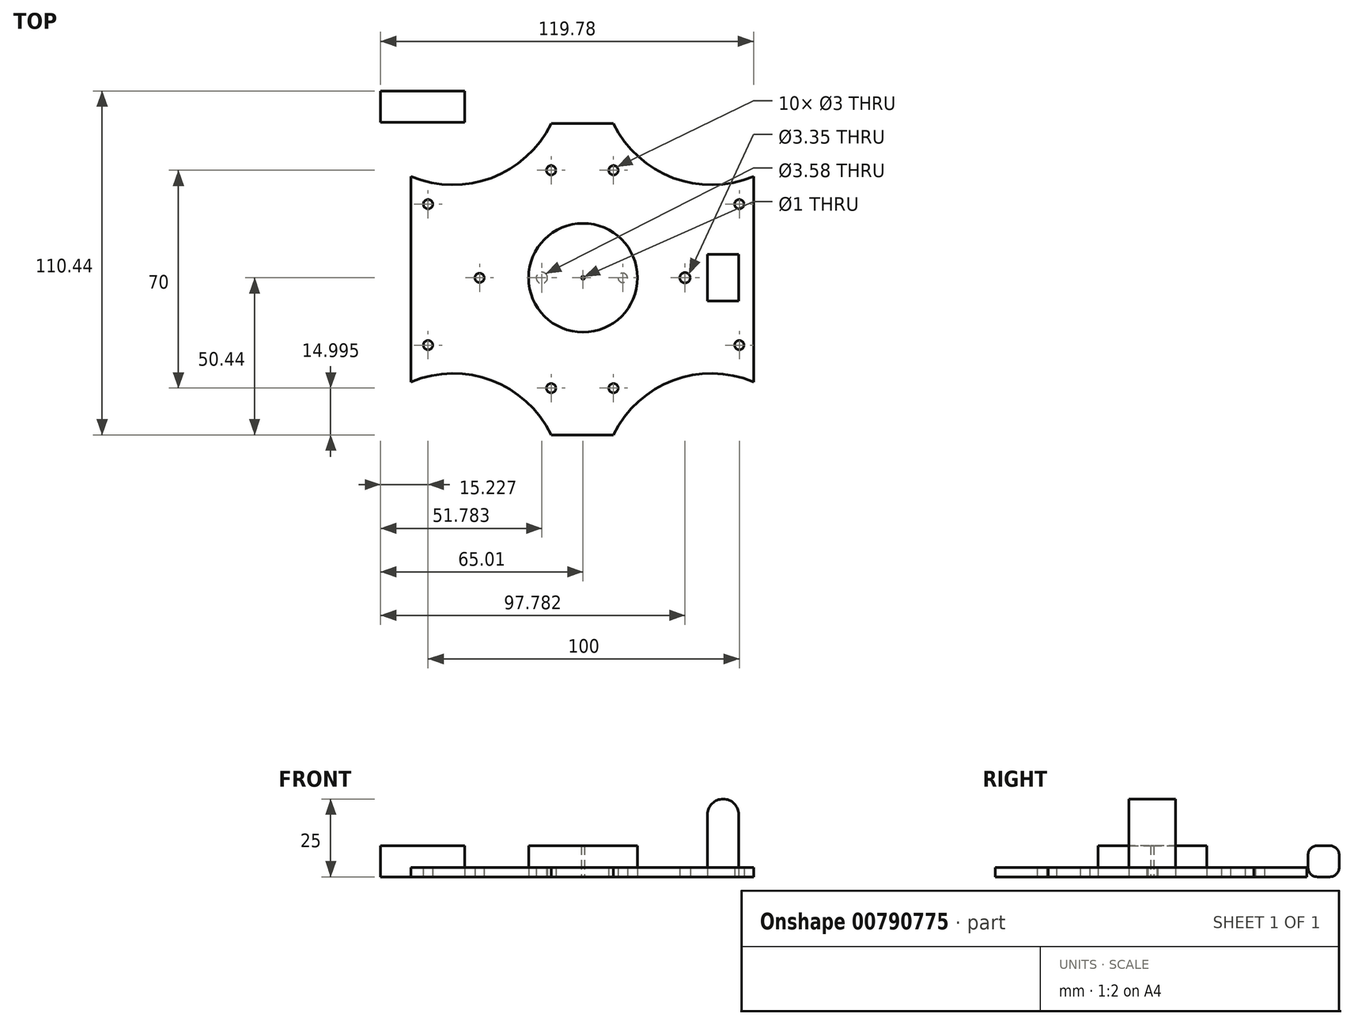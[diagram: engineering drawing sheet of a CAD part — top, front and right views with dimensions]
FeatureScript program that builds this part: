
annotation { "Feature Type Name" : "Feature", "Feature Type Description" : "" }
export const myFeature = defineFeature(function(context is Context, id is Id, definition is map)
    precondition{}
    {
        {
            var Q0;
            Q0=qCreatedBy(makeId("Top.planeOp"),FACE);
            var sketch = newSketch(context, id + "F0", { "sketchPlane" : qUnion([Q0])});
            skCircle(sketch, "E0", {"center": v(0, 0) * mm, "radius": 17.5 * mm});
            skCircle(sketch, "E1", {"center": v(0, 0) * mm, "radius": 0.5 * mm});
            skSolve(sketch);
        }
        {
            var Q0;
            Q0=makeQuery(id+"F0.imprint","IMPRINT",FACE,{"disambiguationData":[TD([[makeQuery(id+"F0.imprint","IMPRINT",EDGE,{"derivedFrom":sQuery(id+"F0.wireOp",EDGE,"E0")}),1.0]])]});
            extrude(context, id + "F1", {"entities" : qUnion([Q0]), "depth" : 10 * mm, "offsetDistance" : 25 * mm});
        }
        {
            var Q0;
            Q0=qCreatedBy(makeId("Top.planeOp"),FACE);
            var sketch = newSketch(context, id + "F2", { "sketchPlane" : qUnion([Q0])});
            skLineSegment(sketch, "E2.bottom", {"start": v(-38.01, 50) * mm, "end": v(-65.01, 50) * mm});
            skLineSegment(sketch, "E2.top", {"start": v(-38.01, 60) * mm, "end": v(-65.01, 60) * mm});
            skLineSegment(sketch, "E2.left", {"start": v(-38.01, 50) * mm, "end": v(-38.01, 60) * mm});
            skLineSegment(sketch, "E2.right", {"start": v(-65.01, 50) * mm, "end": v(-65.01, 60) * mm});
            skPoint(sketch, "E2.middle", {"position": v(-51.51, 55) * mm});
            skSolve(sketch);
        }
        {
            var Q0;
            Q0=makeQuery(id+"F2.imprint","IMPRINT",FACE,{"disambiguationData":[TD([[makeQuery(id+"F2.imprint","IMPRINT",EDGE,{"derivedFrom":sQuery(id+"F2.wireOp",EDGE,"E2.bottom")}),-1.0]])]});
            extrude(context, id + "F3", {"entities" : qUnion([Q0]), "depth" : 10 * mm, "offsetDistance" : 25 * mm});
        }
        {
            var Q0;
            Q0=makeQuery(id+"F3.opExtrude","CAP_EDGE",EDGE,{"disambiguationData":[OSD([sQuery(id+"F2.wireOp",EDGE,"E2.top")])],"isStart":false});
            var Q1;
            Q1=makeQuery(id+"F3.opExtrude","CAP_EDGE",EDGE,{"disambiguationData":[OSD([sQuery(id+"F2.wireOp",EDGE,"E2.bottom")])],"isStart":false});
            var Q2;
            Q2=makeQuery(id+"F3.opExtrude","CAP_EDGE",EDGE,{"disambiguationData":[OSD([sQuery(id+"F2.wireOp",EDGE,"E2.bottom")])],"isStart":true});
            var Q3;
            Q3=makeQuery(id+"F3.opExtrude","CAP_EDGE",EDGE,{"disambiguationData":[OSD([sQuery(id+"F2.wireOp",EDGE,"E2.top")])],"isStart":true});
            fillet(context, id + "F4", {"entities" : qUnion([Q0, Q1, Q2, Q3]), "radius" : 3 * mm, "tangentPropagation" : true, "allowEdgeOverflow" : false});
        }
        {
            var Q0;
            Q0=qCreatedBy(makeId("Top.planeOp"),FACE);
            var sketch = newSketch(context, id + "F5", { "sketchPlane" : qUnion([Q0])});
            skLineSegment(sketch, "E3.bottom", {"start": v(9.77, 49.56) * mm, "end": v(-10.23, 49.56) * mm});
            skLineSegment(sketch, "E3.top", {"start": v(9.77, -50.44) * mm, "end": v(-10.23, -50.44) * mm});
            skLineSegment(sketch, "E3.left", {"start": v(54.77, 32.56) * mm, "end": v(54.77, -33.44) * mm});
            skLineSegment(sketch, "E3.right", {"start": v(-55.23, 32.56) * mm, "end": v(-55.23, -33.44) * mm});
            skPoint(sketch, "E3.middle", {"position": v(0, 0) * mm});
            skPoint(sketch, "E4", {"position": v(-10.23, 49.56) * mm});
            skPoint(sketch, "E5", {"position": v(9.77, 49.56) * mm});
            skPoint(sketch, "E6", {"position": v(-10.23, -50.44) * mm});
            skPoint(sketch, "E7", {"position": v(9.77, -50.44) * mm});
            skPoint(sketch, "E8", {"position": v(54.77, 32.56) * mm});
            skPoint(sketch, "E9", {"position": v(54.77, -33.44) * mm});
            skPoint(sketch, "E10", {"position": v(-55.23, -33.44) * mm});
            skArc(sketch, "E11", {"start": v(-55.23, 32.56) * mm, "mid": v(-29.34, 32.1) * mm, "end": v(-10.23, 49.56) * mm});
            skArc(sketch, "E12", {"start": v(9.77, 49.56) * mm, "mid": v(28.89, 32.1) * mm, "end": v(54.77, 32.56) * mm});
            skArc(sketch, "E13", {"start": v(-10.23, -50.44) * mm, "mid": v(-29.34, -32.99) * mm, "end": v(-55.23, -33.44) * mm});
            skArc(sketch, "E14", {"start": v(54.77, -33.44) * mm, "mid": v(28.89, -32.99) * mm, "end": v(9.77, -50.44) * mm});
            skPoint(sketch, "E15", {"position": v(-33.23, 0) * mm});
            skPoint(sketch, "E16", {"position": v(-13.23, 0) * mm});
            skPoint(sketch, "E17", {"position": v(12.77, 0) * mm});
            skPoint(sketch, "E18", {"position": v(32.77, 0) * mm});
            skPoint(sketch, "E19", {"position": v(-49.78, 23.65) * mm});
            skPoint(sketch, "E20", {"position": v(-49.78, -21.63) * mm});
            skPoint(sketch, "E21", {"position": v(50.22, -21.63) * mm});
            skPoint(sketch, "E22", {"position": v(50.22, 23.65) * mm});
            skCircle(sketch, "E23", {"center": v(-49.78, 23.65) * mm, "radius": 1.5 * mm});
            skCircle(sketch, "E24", {"center": v(-33.23, 0) * mm, "radius": 1.5 * mm});
            skCircle(sketch, "E25", {"center": v(-13.23, 0) * mm, "radius": 1.79 * mm});
            skCircle(sketch, "E26", {"center": v(12.77, 0) * mm, "radius": 1.5 * mm});
            skCircle(sketch, "E27", {"center": v(32.77, 0) * mm, "radius": 1.68 * mm});
            skCircle(sketch, "E28", {"center": v(50.22, -21.63) * mm, "radius": 1.5 * mm});
            skCircle(sketch, "E29", {"center": v(-49.78, -21.63) * mm, "radius": 1.5 * mm});
            skCircle(sketch, "E30", {"center": v(50.22, 23.65) * mm, "radius": 1.5 * mm});
            skPoint(sketch, "E31", {"position": v(-10.23, 34.56) * mm});
            skPoint(sketch, "E32", {"position": v(9.77, 34.56) * mm});
            skPoint(sketch, "E33", {"position": v(-10.23, -35.44) * mm});
            skPoint(sketch, "E34", {"position": v(9.77, -35.44) * mm});
            skCircle(sketch, "E35", {"center": v(-10.23, -35.44) * mm, "radius": 1.5 * mm});
            skCircle(sketch, "E36", {"center": v(9.77, -35.44) * mm, "radius": 1.5 * mm});
            skCircle(sketch, "E37", {"center": v(9.77, 34.56) * mm, "radius": 1.5 * mm});
            skCircle(sketch, "E38", {"center": v(-10.23, 34.56) * mm, "radius": 1.5 * mm});
            skSolve(sketch);
        }
        {
            var Q0;
            Q0 = qSketchRegion(id + "F5", true);
            extrude(context, id + "F6", {"entities" : qUnion([Q0]), "depth" : 3 * mm, "offsetDistance" : 25 * mm});
        }
        {
            var Q0;
            Q0=qCreatedBy(makeId("Top.planeOp"),FACE);
            var sketch = newSketch(context, id + "F7", { "sketchPlane" : qUnion([Q0])});
            skLineSegment(sketch, "E39.bottom", {"start": v(40, 7.5) * mm, "end": v(50, 7.5) * mm});
            skLineSegment(sketch, "E39.top", {"start": v(40, -7.5) * mm, "end": v(50, -7.5) * mm});
            skLineSegment(sketch, "E39.left", {"start": v(40, 7.5) * mm, "end": v(40, -7.5) * mm});
            skLineSegment(sketch, "E39.right", {"start": v(50, 7.5) * mm, "end": v(50, -7.5) * mm});
            skPoint(sketch, "E39.middle", {"position": v(45, 0) * mm});
            skSolve(sketch);
        }
        {
            var Q0;
            Q0 = qSketchRegion(id + "F7", true);
            extrude(context, id + "F8", {"entities" : qUnion([Q0]), "depth" : 25 * mm, "offsetDistance" : 25 * mm});
        }
        {
            var Q0;
            Q0=makeQuery(id+"F8.opExtrude","CAP_EDGE",EDGE,{"disambiguationData":[OSD([sQuery(id+"F7.wireOp",EDGE,"E39.right")])],"isStart":false});
            var Q1;
            Q1=makeQuery(id+"F8.opExtrude","CAP_EDGE",EDGE,{"disambiguationData":[OSD([sQuery(id+"F7.wireOp",EDGE,"E39.left")])],"isStart":false});
            fillet(context, id + "F9", {"entities" : qUnion([Q0, Q1]), "radius" : 5 * mm, "tangentPropagation" : true, "allowEdgeOverflow" : false});
        }
    });
